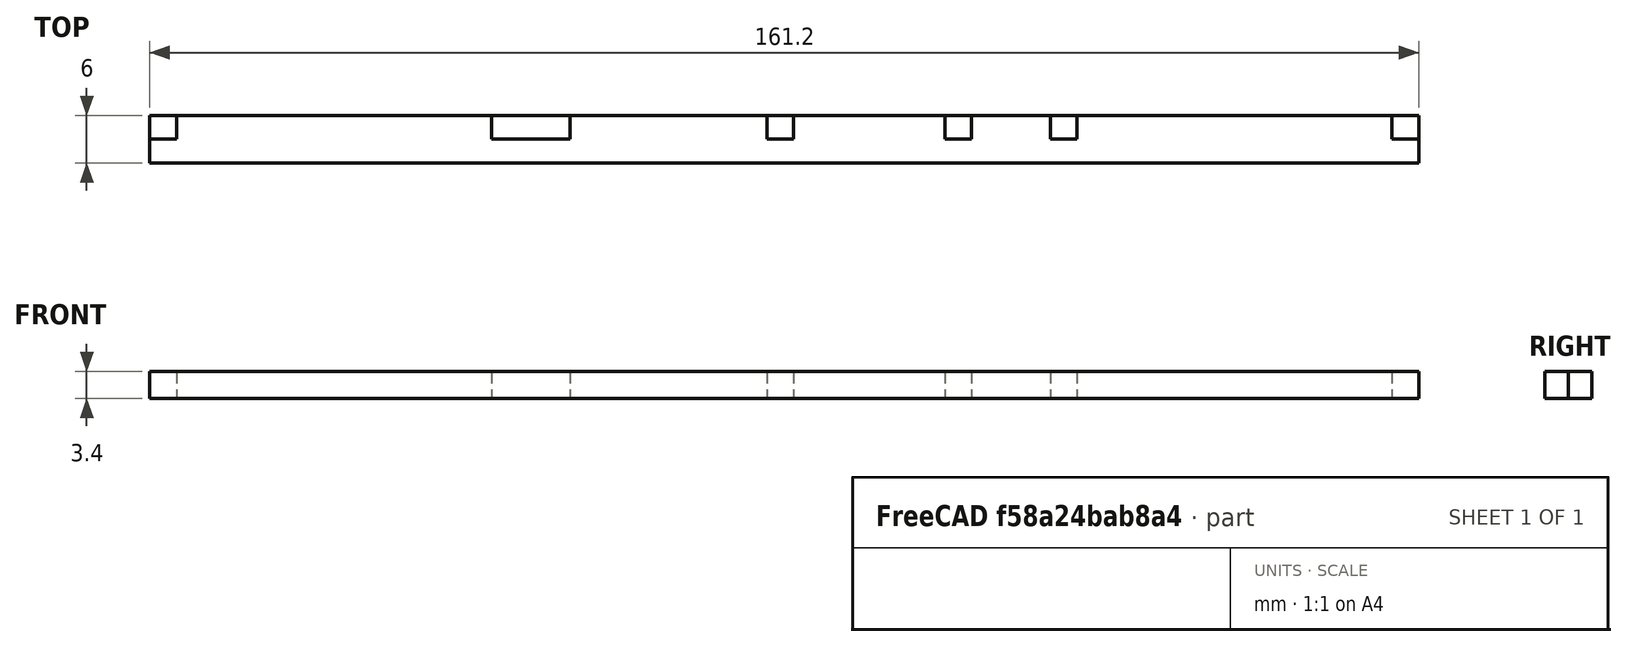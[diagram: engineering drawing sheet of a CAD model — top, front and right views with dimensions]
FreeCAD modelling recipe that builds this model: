
FCSTD DOCUMENT  (FreeCAD 0.17R12703 (Git))
Label: Stringer
License: All rights reserved
LicenseURL: http://en.wikipedia.org/wiki/All_rights_reserved
objects: Path::FeaturePython×5, Part::FeaturePython×2, Part::Feature×1, App::FeaturePython×1, Path::FeatureCompoundPython×1
note: 4 computed .brp shape members not serialized (recipe doc carries the construction recipe); baked Part::Feature solids carry a one-line shape summary decoded from their .brp

FEATURE [Part::Feature] Part__Feature  label="Stringer"
  Placement = pos=(0,0,-3.4) rot=(0,0,1;0rad)
  shape: bbox 161.2 x 6 x 3.4 mm, 26 faces (baked)
FEATURE [App::FeaturePython] SetupSheet  # Path/CAM operation (typed FeaturePython)
  ClearanceHeightExpression = StartDepth+SetupSheet.ClearanceHeightOffset
  ClearanceHeightOffset = 5
  FinalDepthExpression = OpFinalDepth
  HorizRapid = 0
  SafeHeightExpression = StartDepth+SetupSheet.SafeHeightOffset
  SafeHeightOffset = 3
  StartDepthExpression = OpStartDepth
  StepDownExpression = OpToolDiameter
  VertRapid = 0
FEATURE [Part::FeaturePython] Clone  label="Base-Stringer"  # Draft clone (typed FeaturePython)
  AttacherType = Attacher::AttachEngine3D
  Fuse = false
  Objects = -> [Part__Feature]
  PathResource = Base
  Placement = pos=(0,0,-3.4) rot=(0,0,1;0rad)
  Scale = (1,1,1)
FEATURE [Part::FeaturePython] Stock  # WARN: FeaturePython — macro-defined, semantics opaque (R4)
  Base = -> Part__Feature
  ExtXneg = 0
  ExtXpos = 0
  ExtYneg = 0
  ExtYpos = 0
  ExtZneg = 0
  ExtZpos = 0
  StockType = FromBase
FEATURE [Path::FeaturePython] T1__Schaftfraeser_D2  label="T1: Schaftfraeser_D2"  # Path/CAM operation (typed FeaturePython)
  HorizFeed = 400
  HorizRapid = 0
  SpindleDir = 0
  SpindleSpeed = 0
  ToolNumber = 1
  VertFeed = 100
  VertRapid = 0
  expr: HorizRapid = SetupSheet.HorizRapid
  expr: VertRapid = SetupSheet.VertRapid
FEATURE [Path::FeaturePython] Contour  # Path/CAM operation (typed FeaturePython)
  Active = true
  AreaParams:
    OpenMode = 0
    Angle = 45.0
    MinArcPoints = 4
    Coplanar = 2
    Tolerance = 1e-07
    CleanDistance = 0.0
    PocketExtraOffset = 0.0
    AngleShift = 0.0
    SubjectFill = 0
    RoundPreceision = 0.0
    Simplify = False
    SectionTolerance = 1e-06
    MaxArcPoints = 100
    SectionOffset = 0.0
    Offset = 1.0
    Accuracy = 0.01
    PocketStepover = 0.0
    ClipFill = 0
    ToolRadius = 1.0
    Outline = False
    ClipperScale = 10000000.0
    FromCenter = False
    Explode = False
    EndType = 0
    Shift = 0.0
    ExtraPass = 0
    Project = False
    JoinType = 0
    Thicken = False
    Stepdown = 1.0
    SectionMode = 2
    MiterLimit = 2.0
    Deflection = 0.01
    Reorient = True
    FitArcs = True
    SectionCount = -1
    PocketMode = 0
    Stepover = 0.0
    Unit = 1.0
    Fill = 0
  ClearanceHeight = 5
  Direction = 1
  FinalDepth = -3.7
  JoinType = 0
  MiterLimit = 0.1
  OffsetExtra = 0
  OpFinalDepth = -3.4
  OpStartDepth = 0
  OpToolDiameter = 2
  PathParams = {'resume_height': 3.0, 'feedrate': 400.0, 'verbose': True, 'orientation': 0, 'return_end': True, 'preamble': False, 'retraction': 5.0, 'feedrate_v': 100.0}
  SafeHeight = 3
  Side = 0
  StartDepth = 0
  StartPoint = (0,0,0)
  StepDown = 2
  ToolController = -> T1__Schaftfraeser_D2
  UseComp = true
  UseStartPoint = false
  expr: ClearanceHeight = StartDepth + SetupSheet.ClearanceHeightOffset
  expr: SafeHeight = StartDepth + SetupSheet.SafeHeightOffset
  expr: StepDown = 2
  expr: FinalDepth = -3.7000000000000002
  expr: StartDepth = OpStartDepth
FEATURE [Path::FeaturePython] DogboneDressup  # Path/CAM operation (typed FeaturePython)
  Base = -> Contour
  Custom = 0
  Incision = 0
  Side = 0
  Style = 0
  ToolController = -> T1__Schaftfraeser_D2
FEATURE [Path::FeaturePython] TagDressup  # Path/CAM operation (typed FeaturePython)
  Angle = 45
  Base = -> DogboneDressup
  Height = 1.6
  Positions = (3) [(138.335,7,0),(23.4,7,0),(77.5226,-1,0)]
  Radius = 0
  SegmentationFactor = 50
  Width = 4
FEATURE [Path::FeatureCompoundPython] Operations  # Path/CAM operation (typed FeaturePython)
  Group = -> [TagDressup]
  UsePlacements = false
FEATURE [Path::FeaturePython] Job  # Path/CAM operation (typed FeaturePython)
  Base = -> Clone
  GeometryTolerance = 0.01
  Operations = -> Operations
  PostProcessor = 5
  SetupSheet = -> SetupSheet
  Stock = -> Stock
  ToolController = -> [T1__Schaftfraeser_D2]
